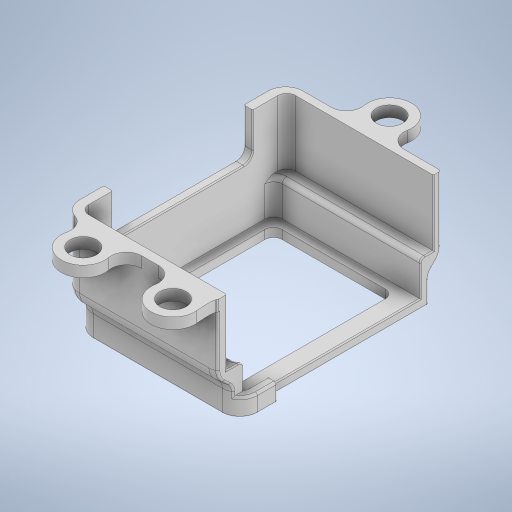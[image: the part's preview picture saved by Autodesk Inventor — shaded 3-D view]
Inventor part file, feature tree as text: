
AUTODESK INVENTOR PART (.ipt)
format: ipt  version: 2023 (Build 270158000, 158)  size: 809,472 bytes
history: native  units: in
note: dims shown in document units (in); Inventor stores cm internally (conversion verified against a paired STEP export)
features: extrude x8, fillet x8, sketch x3, chamfer x2, projected_geometry x2, plane x1
ambient origin geometry x8: Origin, YZ Plane, XZ Plane, XY Plane, X Axis, Y Axis, Z Axis, Center Point
bodies: Body1 (feature_tree)
feature tree (24):
  extrude  "Extrusion3"  Depth=0.0787in
  plane  "Work Plane1"
  extrude  "Extrusion4"  Depth=0.0787in TaperAngle=0.0deg
  extrude  "Extrusion7"  Depth=0.0787in TaperAngle=0.0deg
  extrude  "Extrusion8"  Depth=0.0098in TaperAngle=0.0deg
  extrude  "Extrusion10"  Depth=0.3937in
  extrude  "Extrusion11"  Depth=0.0098in
  extrude  "Extrusion12"  Depth=0.3937in
  extrude  "Extrusion13"  Depth=0.0098in
  chamfer  "Chamfer1"  Distance=0.3937in
  fillet  "Fillet1"  Radius=0.8071in
  fillet  "Fillet2"  Radius=0.0984in
  chamfer  "Chamfer2"  Distance=0.1575in
  fillet  "Fillet3"  Radius=1.4646in
  fillet  "Fillet4"  Radius=1.0827in
  fillet  "Fillet5"  Radius=0.1575in
  fillet  "Fillet6"  Radius=0.0787in
  fillet  "Fillet7"  Radius=0.0787in
  fillet  "Fillet8"  Radius=0.0787in
  sketch  "Sketch6"  dims[d8=0.0787in d9=0.0787in]
  projected_geometry  "Projected Loop3"
  sketch  "Sketch7"  dims[d10=0.0787in d11=0.0in d12=0.315in d13=0.0in]
  sketch  "Sketch8"  dims[d14=0.315in d28=0.0787in d29=0.0in d30=0.5906in d31=0.0in d34=0.3937in d35=0.2362in d40=0.3937in d41=0.2362in d44=0.3937in d45=0.2362in d49=0.8071in d50=0.0984in d51=0.0in d52=0.1575in d53=1.4646in d54=1.0827in d55=0.1575in d56=0.0787in d57=0.0787in d58=0.0in d59=0.0787in d61=1.2598in d64=0.2362in d65=0.0in d66=0.0787in d67=0.0787in d68=0.1772in d69=0.1575in d70=0.2362in d71=0.0in d79=1.6929in d80=1.2402in d81=0.1575in d83=0.187in d85=0.0394in d87=0.0394in d89=0.7382in d90=0.2165in d91=0.3937in d93=0.1378in d94=0.1378in d96=0.1575in d97=0.1378in d98=0.3859in d99=0.1378in d100=0.1378in d101=0.0787in d102=0.0787in d103=45.0deg d104=0.1378in d105=0.0984in d106=0.0787in d107=0.0787in d108=45.0deg d109=0.0984in d110=0.1378in d111=0.0197in d112=0.0394in d113=0.0098in d114=0.0098in d116=0.0197in d117=0.0591in d118=0.187in]
  projected_geometry  "Projected Loop4"
